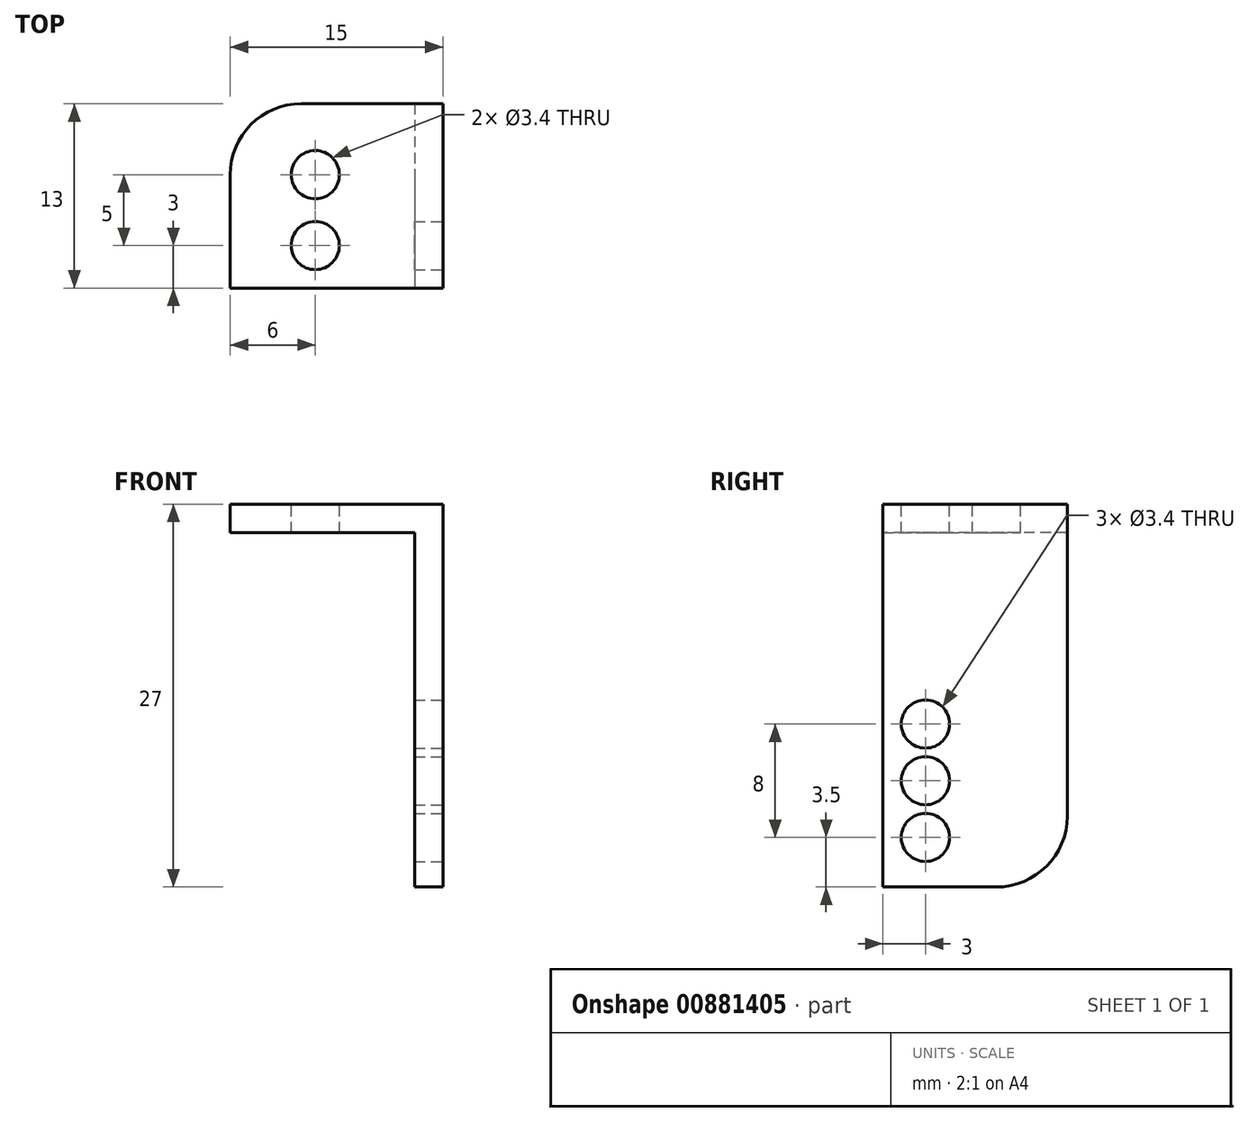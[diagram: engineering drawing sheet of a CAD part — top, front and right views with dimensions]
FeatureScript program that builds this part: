
annotation { "Feature Type Name" : "Feature", "Feature Type Description" : "" }
export const myFeature = defineFeature(function(context is Context, id is Id, definition is map)
    precondition{}
    {
        {
            var Q0;
            Q0=qCreatedBy(makeId("Top.planeOp"),FACE);
            var sketch = newSketch(context, id + "F0", { "sketchPlane" : qUnion([Q0])});
            skLineSegment(sketch, "E0.bottom", {"start": v(7.5, -10) * mm, "end": v(-7.5, -10) * mm});
            skLineSegment(sketch, "E0.top", {"start": v(7.5, 10) * mm, "end": v(-7.5, 10) * mm});
            skLineSegment(sketch, "E0.left", {"start": v(7.5, -10) * mm, "end": v(7.5, 10) * mm});
            skLineSegment(sketch, "E0.right", {"start": v(-7.5, -10) * mm, "end": v(-7.5, 10) * mm});
            skPoint(sketch, "E0.middle", {"position": v(0, 0) * mm});
            skPoint(sketch, "E1", {"position": v(-1.5, 5) * mm});
            skPoint(sketch, "E2", {"position": v(-1.5, 0) * mm});
            skPoint(sketch, "E3", {"position": v(-1.5, -5) * mm});
            skPoint(sketch, "E4", {"position": v(5.5, 10) * mm});
            skPoint(sketch, "E5", {"position": v(5.5, -10) * mm});
            skLineSegment(sketch, "E6", {"start": v(5.5, 10) * mm, "end": v(5.5, -10) * mm});
            skSolve(sketch);
        }
        {
            var Q0;
            Q0=makeQuery(id+"F0.imprint","IMPRINT",FACE,{"disambiguationData":[TD([[makeQuery(id+"F0.imprint","IMPRINT",EDGE,{"derivedFrom":sQuery(id+"F0.wireOp",EDGE,"E0.bottom")}),-1.0]])]});
            extrude(context, id + "F1", {"entities" : qUnion([Q0]), "depth" : 2 * mm, "offsetDistance" : 25 * mm});
        }
        {
            var Q0;
            Q0=sQuery(id+"F0.wireOp",VERTEX,"E1");
            var Q1;
            Q1=sQuery(id+"F0.wireOp",VERTEX,"E2");
            var Q2;
            Q2=sQuery(id+"F0.wireOp",VERTEX,"E3");
            var Q3;
            Q3=makeQuery(id+"F1.opExtrude","SWEPT_BODY",BODY,{"disambiguationData":[OSD([sQuery(id+"F0.wireOp",EDGE,"E0.bottom"),sQuery(id+"F0.wireOp",EDGE,"E0.top"),sQuery(id+"F0.wireOp",EDGE,"E0.left"),sQuery(id+"F0.wireOp",EDGE,"E0.right")])]});
            hole(context, id + "F2", {"style" : HoleStyle.SIMPLE, "endStyle" : HoleEndStyle.THROUGH, "oppositeDirection" : true, "standardTappedOrClearance" : lookupTablePath({ "fit" : "Normal", "standard" : "ISO", "size" : "M3", "type" : "Clearance" }), "standardBlindInLast" : lookupTablePath({ "fit" : "Normal", "standard" : "ISO", "engagement" : "75%", "pitch" : "0.5 mm", "size" : "M3", "type" : "Clearance & tapped" }), "holeDiameter" : 3.4 * mm, "majorDiameter" : 5 * mm, "isTappedThrough" : true, "tappedDepth" : 12 * mm, "tapClearance" : 3, "locations" : qUnion([Q0, Q1, Q2]), "scope" : qUnion([Q3]), "startStyle" : HoleStartStyle.SKETCH});
        }
        {
            var Q0;
            {var subQ2=sQuery(id+"F0.wireOp",EDGE,"E0.left");Q0=makeQuery(id+"F0.imprint","IMPRINT",FACE,{"disambiguationData":[TD([[makeQuery(id+"F0.imprint","IMPRINT",EDGE,{"derivedFrom":subQ2}),1.0]])]});}
            extrude(context, id + "F3", {"entities" : qUnion([Q0]), "operationType" : NewBodyOperationType.ADD, "oppositeDirection" : true, "depth" : 25 * mm, "offsetDistance" : 25 * mm});
        }
        {
            var Q0;
            Q0=makeQuery(id+"F3.opExtrude","SWEPT_FACE",FACE,{"disambiguationData":[OSD([sQuery(id+"F0.wireOp",EDGE,"E6")])]});
            var sketch = newSketch(context, id + "F4", { "sketchPlane" : qUnion([Q0])});
            skPoint(sketch, "E7", {"position": v(0, -17.5) * mm});
            skPoint(sketch, "E8", {"position": v(0, -13.5) * mm});
            skPoint(sketch, "E9", {"position": v(0, -21.5) * mm});
            skSolve(sketch);
        }
        {
            var Q0;
            Q0=sQuery(id+"F4.wireOp",VERTEX,"E7");
            var Q1;
            Q1=sQuery(id+"F4.wireOp",VERTEX,"E8");
            var Q2;
            Q2=sQuery(id+"F4.wireOp",VERTEX,"E9");
            var Q3;
            Q3=makeQuery(id+"F1.opExtrude","SWEPT_BODY",BODY,{"disambiguationData":[OSD([sQuery(id+"F0.wireOp",EDGE,"E0.bottom"),sQuery(id+"F0.wireOp",EDGE,"E0.top"),sQuery(id+"F0.wireOp",EDGE,"E0.left"),sQuery(id+"F0.wireOp",EDGE,"E0.right")])]});
            hole(context, id + "F5", {"style" : HoleStyle.SIMPLE, "endStyle" : HoleEndStyle.THROUGH, "standardTappedOrClearance" : lookupTablePath({ "fit" : "Normal", "standard" : "ISO", "size" : "M3", "type" : "Clearance" }), "standardBlindInLast" : lookupTablePath({ "fit" : "Normal", "standard" : "ISO", "engagement" : "75%", "pitch" : "0.5 mm", "size" : "M3", "type" : "Clearance & tapped" }), "holeDiameter" : 3.4 * mm, "majorDiameter" : 5 * mm, "isTappedThrough" : true, "tappedDepth" : 12 * mm, "tapClearance" : 3, "locations" : qUnion([Q0, Q1, Q2]), "scope" : qUnion([Q3]), "startStyle" : HoleStartStyle.SKETCH});
        }
        {
            var Q0;
            {var subQ0=sQuery(id+"F0.wireOp",EDGE,"E0.bottom");Q0=makeQuery(id+"F3.boolean.opBoolean","MERGE",FACE,{"derivedFrom":[makeQuery(id+"F1.opExtrude","SWEPT_FACE",FACE,{"disambiguationData":[OSD([subQ0])]}),makeQuery(id+"F3.opExtrude","SWEPT_FACE",FACE,{"disambiguationData":[OSD([subQ0])]})]});}
            extrude(context, id + "F6", {"entities" : qUnion([Q0]), "operationType" : NewBodyOperationType.REMOVE, "oppositeDirection" : true, "depth" : 7 * mm, "offsetDistance" : 25 * mm});
        }
        {
            var Q0;
            {var subQ0=sQuery(id+"F0.wireOp",EDGE,"E0.top");Q0=makeQuery(id+"F6.boolean.opBoolean","COPY",EDGE,{"derivedFrom":makeQuery(id+"F6.opExtrude","CAP_EDGE",EDGE,{"disambiguationData":[OSD([subQ0]),TDD([makeQuery(id+"F3.opExtrude","CAP_EDGE",EDGE,{"disambiguationData":[OSD([subQ0])],"isStart":false})])],"isStart":false})});}
            var Q1;
            Q1=makeQuery(id+"F3.opExtrude","CAP_EDGE",EDGE,{"disambiguationData":[OSD([sQuery(id+"F0.wireOp",EDGE,"E0.bottom")])],"isStart":false});
            var Q2;
            Q2=makeQuery(id+"F1.opExtrude","SWEPT_EDGE",EDGE,{"disambiguationData":[OSD([sQuery(id+"F0.wireOp",EDGE,"E0.bottom"),sQuery(id+"F0.wireOp",EDGE,"E0.right")])]});
            var Q3;
            Q3=makeQuery(id+"F6.boolean.opBoolean","COPY",EDGE,{"derivedFrom":makeQuery(id+"F6.opExtrude","CAP_EDGE",EDGE,{"disambiguationData":[OSD([sQuery(id+"F0.wireOp",EDGE,"E0.top"),sQuery(id+"F0.wireOp",EDGE,"E0.right")])],"isStart":false})});
            var Q4;
            Q4=makeQuery(id+"F1.opExtrude","SWEPT_EDGE",EDGE,{"disambiguationData":[OSD([sQuery(id+"F0.wireOp",EDGE,"E0.top"),sQuery(id+"F0.wireOp",EDGE,"E0.right")])]});
            var Q5;
            Q5=makeQuery(id+"F3.opExtrude","CAP_EDGE",EDGE,{"disambiguationData":[OSD([sQuery(id+"F0.wireOp",EDGE,"E0.top")])],"isStart":false});
            var Q6;
            {var subQ0=sQuery(id+"F0.wireOp",EDGE,"E0.bottom");Q6=makeQuery(id+"F6.boolean.opBoolean","COPY",EDGE,{"derivedFrom":makeQuery(id+"F6.opExtrude","CAP_EDGE",EDGE,{"disambiguationData":[OSD([subQ0]),TDD([makeQuery(id+"F3.opExtrude","CAP_EDGE",EDGE,{"disambiguationData":[OSD([subQ0])],"isStart":false})])],"isStart":false})});}
            fillet(context, id + "F7", {"entities" : qUnion([Q0, Q1, Q2, Q3, Q4, Q5, Q6]), "tangentPropagation" : true, "radius" : 5 * mm, "defaultsChanged" : false, "vertexSettings" : [], "allowEdgeOverflow" : false});
        }
    });
